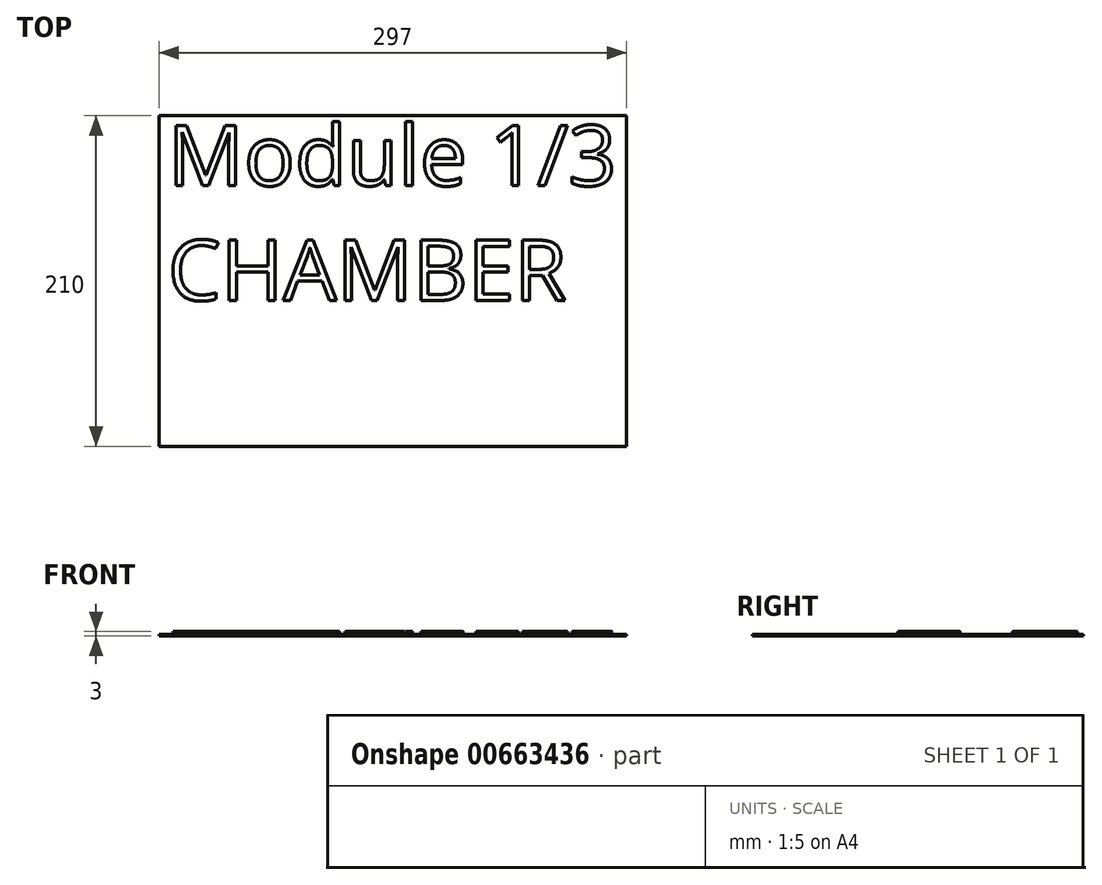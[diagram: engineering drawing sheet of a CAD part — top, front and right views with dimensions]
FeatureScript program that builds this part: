
annotation { "Feature Type Name" : "Feature", "Feature Type Description" : "" }
export const myFeature = defineFeature(function(context is Context, id is Id, definition is map)
    precondition{}
    {
        {
            var Q0;
            Q0=qCreatedBy(makeId("Top.planeOp"),FACE);
            var sketch = newSketch(context, id + "F0", { "sketchPlane" : qUnion([Q0])});
            skLineSegment(sketch, "E0.bottom", {"start": v(-195.9, 139.38) * mm, "end": v(101.1, 139.38) * mm});
            skLineSegment(sketch, "E0.top", {"start": v(-195.9, -70.62) * mm, "end": v(101.1, -70.62) * mm});
            skLineSegment(sketch, "E0.left", {"start": v(-195.9, 139.38) * mm, "end": v(-195.9, -70.62) * mm});
            skLineSegment(sketch, "E0.right", {"start": v(101.1, 139.38) * mm, "end": v(101.1, -70.62) * mm});
            skSolve(sketch);
        }
        {
            var Q0;
            Q0=qSketchRegion(id+"F0",true);
            extrude(context, id + "F1", {"entities" : qUnion([Q0]), "depth" : 1 * mm, "offsetDistance" : 25 * mm});
        }
        {
            var Q0;
            Q0=makeQuery(id+"F1.opExtrude","CAP_FACE",FACE,{"disambiguationData":[OSD([sQuery(id+"F0.wireOp",EDGE,"E0.bottom"),sQuery(id+"F0.wireOp",EDGE,"E0.top"),sQuery(id+"F0.wireOp",EDGE,"E0.left"),sQuery(id+"F0.wireOp",EDGE,"E0.right")])],"isStart":false});
            var sketch = newSketch(context, id + "F2", { "sketchPlane" : qUnion([Q0])});
            skText(sketch, "E1", { "text": "Module 1/3\nCHAMBER", "fontName": "OpenSans-Regular.ttf"});
            const initialGuessF2  = {"E1": [-0.19035, 0.095, 1, 0, 0.03858]};
            skSetInitialGuess(sketch, initialGuessF2);
            skSolve(sketch);
        }
        {
            var Q0;
            Q0=qSketchRegion(id+"F2",true);
            extrude(context, id + "F3", {"entities" : qUnion([Q0]), "operationType" : NewBodyOperationType.ADD, "depth" : 2 * mm, "offsetDistance" : 25 * mm});
        }
    });
